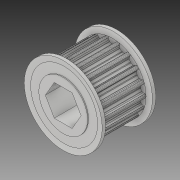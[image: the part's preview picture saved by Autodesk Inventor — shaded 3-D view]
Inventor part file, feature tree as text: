
AUTODESK INVENTOR PART (.ipt)
format: ipt  version: 2019 (Build 230136000, 136)  size: 492,544 bytes
history: native  units: in
note: dims shown in document units (in); Inventor stores cm internally (conversion verified against a paired STEP export)
features: mirror x1
ambient origin geometry x8: Origin, YZ Plane, XZ Plane, XY Plane, X Axis, Y Axis, Z Axis, Center Point
bodies: Solid1 (feature_tree)
feature tree (1):
  mirror  "Mirror1"
